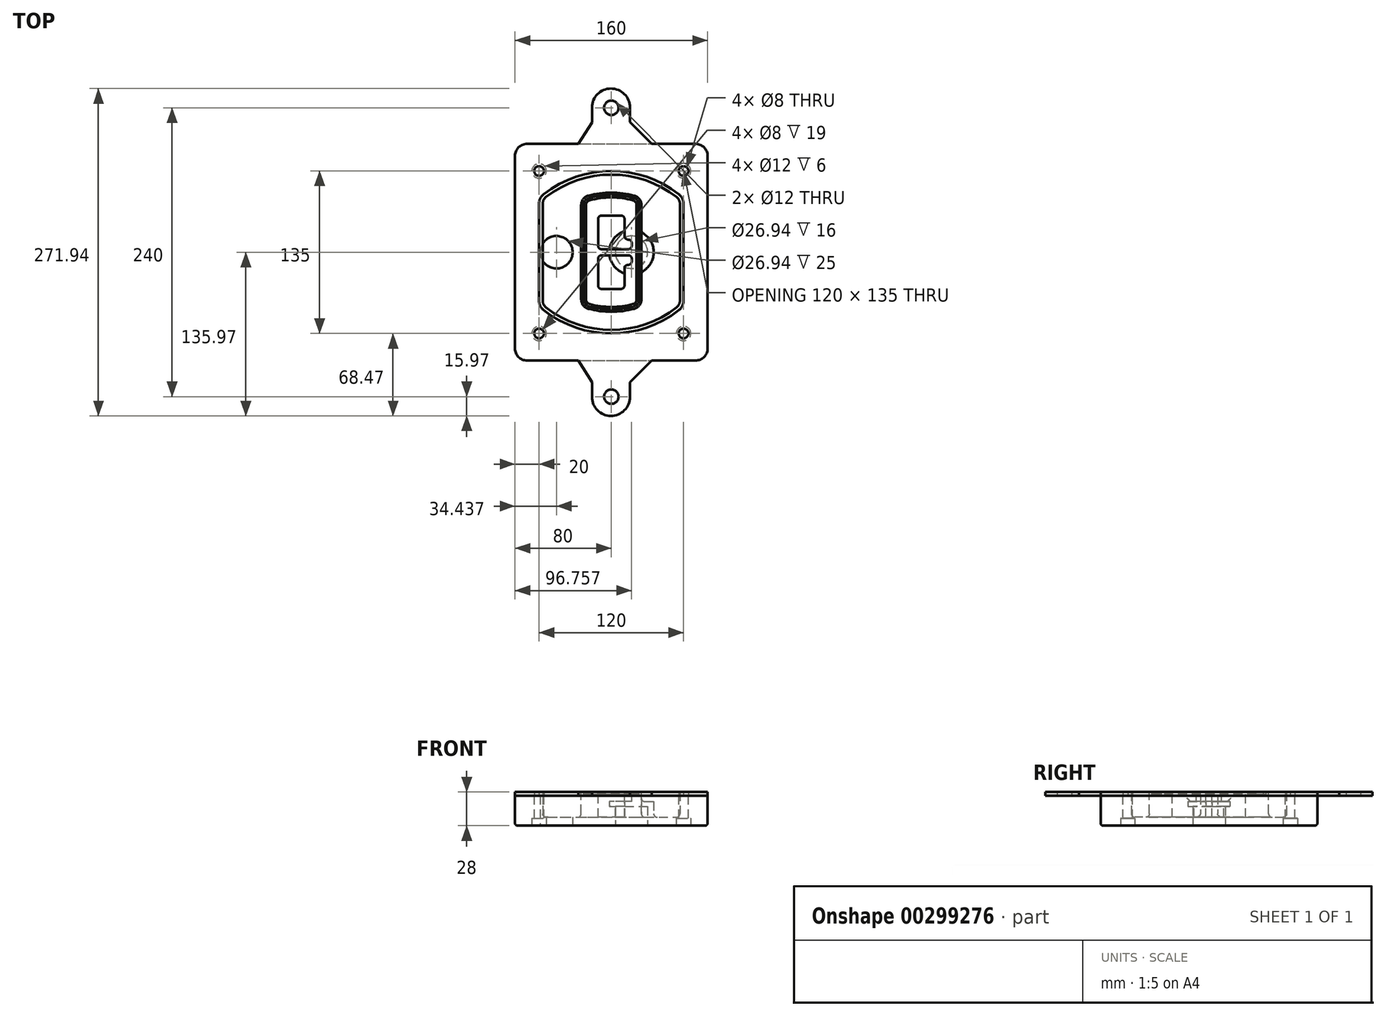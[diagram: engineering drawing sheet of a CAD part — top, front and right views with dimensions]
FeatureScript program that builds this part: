
annotation { "Feature Type Name" : "Feature", "Feature Type Description" : "" }
export const myFeature = defineFeature(function(context is Context, id is Id, definition is map)
    precondition{}
    {
        {
            var Q0;
            Q0=qCreatedBy(makeId("Top.planeOp"),FACE);
            var sketch = newSketch(context, id + "F0", { "sketchPlane" : qUnion([Q0])});
            skPoint(sketch, "E0.rect.middle", {"position": v(0, 0) * mm});
            skLineSegment(sketch, "E1.bottom", {"start": v(-70, -90) * mm, "end": v(70, -90) * mm});
            skLineSegment(sketch, "E1.top", {"start": v(-70, 90) * mm, "end": v(70, 90) * mm});
            skLineSegment(sketch, "E1.left", {"start": v(-80, -80) * mm, "end": v(-80, 80) * mm});
            skLineSegment(sketch, "E1.right", {"start": v(80, -80) * mm, "end": v(80, 80) * mm});
            skLineSegment(sketch, "E2", {"start": v(-80, 90) * mm, "end": v(80, -90) * mm, "construction": true});
            skLineSegment(sketch, "E3", {"start": v(80, 90) * mm, "end": v(-80, -90) * mm, "construction": true});
            skCircle(sketch, "E4", {"center": v(-60, 67.5) * mm, "radius": 4 * mm});
            skCircle(sketch, "E5", {"center": v(60, 67.5) * mm, "radius": 4 * mm});
            skCircle(sketch, "E6", {"center": v(60, -67.5) * mm, "radius": 4 * mm});
            skCircle(sketch, "E7", {"center": v(-60, -67.5) * mm, "radius": 4 * mm});
            skLineSegment(sketch, "E8", {"start": v(-60, 67.5) * mm, "end": v(60, 67.5) * mm, "construction": true});
            skLineSegment(sketch, "E9", {"start": v(60, 67.5) * mm, "end": v(60, -67.5) * mm, "construction": true});
            skLineSegment(sketch, "E10", {"start": v(60, -67.5) * mm, "end": v(-60, -67.5) * mm, "construction": true});
            skLineSegment(sketch, "E11", {"start": v(-60, -67.5) * mm, "end": v(-60, 67.5) * mm, "construction": true});
            skLineSegment(sketch, "E12", {"start": v(-60, 40.3) * mm, "end": v(-60, -40.3) * mm});
            skLineSegment(sketch, "E13", {"start": v(60, 40.3) * mm, "end": v(60, -40.3) * mm});
            skArc(sketch, "E14", {"start": v(56.15, 48.18) * mm, "mid": v(0, 67.5) * mm, "end": v(-56.15, 48.18) * mm});
            skArc(sketch, "E15", {"start": v(-56.15, -48.18) * mm, "mid": v(0, -67.5) * mm, "end": v(56.15, -48.18) * mm});
            skLineSegment(sketch, "E16", {"start": v(-60, 0) * mm, "end": v(60, 0) * mm, "construction": true});
            skPoint(sketch, "E17.visualSharp", {"position": v(-60, -45) * mm});
            skArc(sketch, "E17.filletArc", {"start": v(-60, -40.3) * mm, "mid": v(-58.99, -44.68) * mm, "end": v(-56.15, -48.18) * mm});
            skPoint(sketch, "E18.visualSharp", {"position": v(-60, 45) * mm});
            skArc(sketch, "E18.filletArc", {"start": v(-56.15, 48.18) * mm, "mid": v(-58.99, 44.68) * mm, "end": v(-60, 40.3) * mm});
            skPoint(sketch, "E19.visualSharp", {"position": v(60, 45) * mm});
            skArc(sketch, "E19.filletArc", {"start": v(60, 40.3) * mm, "mid": v(58.99, 44.68) * mm, "end": v(56.15, 48.18) * mm});
            skPoint(sketch, "E20.visualSharp", {"position": v(60, -45) * mm});
            skArc(sketch, "E20.filletArc", {"start": v(56.15, -48.18) * mm, "mid": v(58.99, -44.68) * mm, "end": v(60, -40.3) * mm});
            skPoint(sketch, "E21.visualSharp", {"position": v(-80, 90) * mm});
            skArc(sketch, "E21.filletArc", {"start": v(-70, 90) * mm, "mid": v(-77.07, 87.07) * mm, "end": v(-80, 80) * mm});
            skPoint(sketch, "E22.visualSharp", {"position": v(80, 90) * mm});
            skArc(sketch, "E22.filletArc", {"start": v(80, 80) * mm, "mid": v(77.07, 87.07) * mm, "end": v(70, 90) * mm});
            skPoint(sketch, "E23.visualSharp", {"position": v(80, -90) * mm});
            skArc(sketch, "E23.filletArc", {"start": v(70, -90) * mm, "mid": v(77.07, -87.07) * mm, "end": v(80, -80) * mm});
            skPoint(sketch, "E24.visualSharp", {"position": v(-80, -90) * mm});
            skArc(sketch, "E24.filletArc", {"start": v(-80, -80) * mm, "mid": v(-77.07, -87.07) * mm, "end": v(-70, -90) * mm});
            skArc(sketch, "E25.0", {"start": v(57, 40.3) * mm, "mid": v(56.3, 43.36) * mm, "end": v(54.3, 45.81) * mm});
            skLineSegment(sketch, "E25.1", {"start": v(57, 40.3) * mm, "end": v(57, -40.3) * mm});
            skArc(sketch, "E25.2", {"start": v(54.3, -45.81) * mm, "mid": v(56.3, -43.36) * mm, "end": v(57, -40.3) * mm});
            skArc(sketch, "E25.3", {"start": v(-54.3, -45.81) * mm, "mid": v(0, -64.5) * mm, "end": v(54.3, -45.81) * mm});
            skArc(sketch, "E25.4", {"start": v(-57, -40.3) * mm, "mid": v(-56.3, -43.36) * mm, "end": v(-54.3, -45.81) * mm});
            skArc(sketch, "E25.5", {"start": v(54.3, 45.81) * mm, "mid": v(0, 64.5) * mm, "end": v(-54.3, 45.81) * mm});
            skLineSegment(sketch, "E25.6", {"start": v(-57, 40.3) * mm, "end": v(-57, -40.3) * mm});
            skArc(sketch, "E25.7", {"start": v(-54.3, 45.81) * mm, "mid": v(-56.3, 43.36) * mm, "end": v(-57, 40.3) * mm});
            skArc(sketch, "E26.0", {"start": v(-58.62, 51.33) * mm, "mid": v(-62.58, 46.43) * mm, "end": v(-64, 40.3) * mm});
            skArc(sketch, "E26.1", {"start": v(58.62, 51.33) * mm, "mid": v(0, 71.5) * mm, "end": v(-58.62, 51.33) * mm});
            skArc(sketch, "E26.2", {"start": v(64, 40.3) * mm, "mid": v(62.58, 46.43) * mm, "end": v(58.62, 51.33) * mm});
            skLineSegment(sketch, "E26.3", {"start": v(64, 40.3) * mm, "end": v(64, -40.3) * mm});
            skArc(sketch, "E26.4", {"start": v(58.62, -51.33) * mm, "mid": v(62.58, -46.43) * mm, "end": v(64, -40.3) * mm});
            skLineSegment(sketch, "E26.5", {"start": v(-64, 40.3) * mm, "end": v(-64, -40.3) * mm});
            skArc(sketch, "E26.6", {"start": v(-58.62, -51.33) * mm, "mid": v(0, -71.5) * mm, "end": v(58.62, -51.33) * mm});
            skArc(sketch, "E26.7", {"start": v(-64, -40.3) * mm, "mid": v(-62.58, -46.43) * mm, "end": v(-58.62, -51.33) * mm});
            skSolve(sketch);
        }
        {
            var Q0;
            Q0=makeQuery(id+"F0.imprint","IMPRINT",FACE,{"disambiguationData":[TD([[makeQuery(id+"F0.imprint","IMPRINT",EDGE,{"derivedFrom":sQuery(id+"F0.wireOp",EDGE,"E1.bottom")}),1.0]])]});
            var Q1;
            Q1=makeQuery(id+"F0.imprint","IMPRINT",FACE,{"disambiguationData":[TD([[makeQuery(id+"F0.imprint","IMPRINT",EDGE,{"derivedFrom":sQuery(id+"F0.wireOp",EDGE,"E12")}),1.0]])]});
            var Q2;
            Q2=makeQuery(id+"F0.imprint","IMPRINT",FACE,{"disambiguationData":[TD([[makeQuery(id+"F0.imprint","IMPRINT",EDGE,{"derivedFrom":sQuery(id+"F0.wireOp",EDGE,"E25.0")}),1.0]])]});
            var Q3;
            Q3=makeQuery(id+"F0.imprint","IMPRINT",FACE,{"disambiguationData":[TD([[makeQuery(id+"F0.imprint","IMPRINT",EDGE,{"derivedFrom":sQuery(id+"F0.wireOp",EDGE,"E12")}),-1.0]])]});
            extrude(context, id + "F1", {"entities" : qUnion([Q0, Q1, Q2, Q3]), "oppositeDirection" : true, "depth" : 25 * mm});
        }
        {
            var Q0;
            Q0=makeQuery(id+"F0.imprint","IMPRINT",FACE,{"disambiguationData":[TD([[makeQuery(id+"F0.imprint","IMPRINT",EDGE,{"derivedFrom":sQuery(id+"F0.wireOp",EDGE,"E12")}),1.0]])]});
            extrude(context, id + "F2", {"entities" : qUnion([Q0]), "operationType" : NewBodyOperationType.ADD, "depth" : 3 * mm});
        }
        {
            var Q0;
            Q0=makeQuery(id+"F0.imprint","IMPRINT",FACE,{"disambiguationData":[TD([[makeQuery(id+"F0.imprint","IMPRINT",EDGE,{"derivedFrom":sQuery(id+"F0.wireOp",EDGE,"E25.0")}),1.0]])]});
            extrude(context, id + "F3", {"entities" : qUnion([Q0]), "operationType" : NewBodyOperationType.REMOVE, "oppositeDirection" : true, "depth" : 18 * mm});
        }
        {
            var Q0;
            Q0=makeQuery(id+"F2.opExtrude","CAP_FACE",FACE,{"disambiguationData":[OSD([sQuery(id+"F0.wireOp",EDGE,"E12"),sQuery(id+"F0.wireOp",EDGE,"E13"),sQuery(id+"F0.wireOp",EDGE,"E14"),sQuery(id+"F0.wireOp",EDGE,"E15"),sQuery(id+"F0.wireOp",EDGE,"E17.filletArc"),sQuery(id+"F0.wireOp",EDGE,"E18.filletArc"),sQuery(id+"F0.wireOp",EDGE,"E19.filletArc"),sQuery(id+"F0.wireOp",EDGE,"E20.filletArc"),sQuery(id+"F0.wireOp",EDGE,"E25.0"),sQuery(id+"F0.wireOp",EDGE,"E25.1"),sQuery(id+"F0.wireOp",EDGE,"E25.2"),sQuery(id+"F0.wireOp",EDGE,"E25.3"),sQuery(id+"F0.wireOp",EDGE,"E25.4"),sQuery(id+"F0.wireOp",EDGE,"E25.5"),sQuery(id+"F0.wireOp",EDGE,"E25.6"),sQuery(id+"F0.wireOp",EDGE,"E25.7")])],"isStart":false});
            var sketch = newSketch(context, id + "F4", { "sketchPlane" : qUnion([Q0])});
            skArc(sketch, "E27.0", {"start": v(-19.08, -46.97) * mm, "mid": v(0, -49.5) * mm, "end": v(19.08, -46.97) * mm});
            skArc(sketch, "E28.0", {"start": v(19.08, 46.97) * mm, "mid": v(0, 49.5) * mm, "end": v(-19.08, 46.97) * mm});
            skLineSegment(sketch, "E29", {"start": v(-25, 39.25) * mm, "end": v(-25, -39.25) * mm});
            skLineSegment(sketch, "E30", {"start": v(25, 39.25) * mm, "end": v(25, -39.25) * mm});
            skLineSegment(sketch, "E31", {"start": v(-25, 45.1) * mm, "end": v(25, 45.1) * mm, "construction": true});
            skLineSegment(sketch, "E32", {"start": v(-25, -45.1) * mm, "end": v(25, -45.1) * mm, "construction": true});
            skPoint(sketch, "E33.visualSharp", {"position": v(-25, 45.1) * mm});
            skArc(sketch, "E33.filletArc", {"start": v(-19.08, 46.97) * mm, "mid": v(-23.35, 44.11) * mm, "end": v(-25, 39.25) * mm});
            skPoint(sketch, "E34.visualSharp", {"position": v(25, 45.1) * mm});
            skArc(sketch, "E34.filletArc", {"start": v(25, 39.25) * mm, "mid": v(23.35, 44.11) * mm, "end": v(19.08, 46.97) * mm});
            skPoint(sketch, "E35.visualSharp", {"position": v(25, -45.1) * mm});
            skArc(sketch, "E35.filletArc", {"start": v(19.08, -46.97) * mm, "mid": v(23.35, -44.11) * mm, "end": v(25, -39.25) * mm});
            skPoint(sketch, "E36.visualSharp", {"position": v(-25, -45.1) * mm});
            skArc(sketch, "E36.filletArc", {"start": v(-25, -39.25) * mm, "mid": v(-23.35, -44.11) * mm, "end": v(-19.08, -46.97) * mm});
            skArc(sketch, "E37.0", {"start": v(54.3, 45.81) * mm, "mid": v(0, 64.5) * mm, "end": v(-54.3, 45.81) * mm});
            skArc(sketch, "E37.1", {"start": v(-54.3, 45.81) * mm, "mid": v(-56.3, 43.36) * mm, "end": v(-57, 40.3) * mm});
            skLineSegment(sketch, "E37.2", {"start": v(-57, 40.3) * mm, "end": v(-57, -40.3) * mm});
            skArc(sketch, "E37.3", {"start": v(-57, -40.3) * mm, "mid": v(-56.3, -43.36) * mm, "end": v(-54.3, -45.81) * mm});
            skArc(sketch, "E37.4", {"start": v(-54.3, -45.81) * mm, "mid": v(0, -64.5) * mm, "end": v(54.3, -45.81) * mm});
            skArc(sketch, "E37.5", {"start": v(54.3, -45.81) * mm, "mid": v(56.3, -43.36) * mm, "end": v(57, -40.3) * mm});
            skLineSegment(sketch, "E37.6", {"start": v(57, 40.3) * mm, "end": v(57, -40.3) * mm});
            skArc(sketch, "E37.7", {"start": v(57, 40.3) * mm, "mid": v(56.3, 43.36) * mm, "end": v(54.3, 45.81) * mm});
            skLineSegment(sketch, "E38.0", {"start": v(23, 39.25) * mm, "end": v(23, -39.25) * mm});
            skArc(sketch, "E38.1", {"start": v(18.56, -45.04) * mm, "mid": v(21.76, -42.9) * mm, "end": v(23, -39.25) * mm});
            skArc(sketch, "E38.2", {"start": v(-18.56, -45.04) * mm, "mid": v(0, -47.5) * mm, "end": v(18.56, -45.04) * mm});
            skArc(sketch, "E38.3", {"start": v(-23, -39.25) * mm, "mid": v(-21.76, -42.9) * mm, "end": v(-18.56, -45.04) * mm});
            skLineSegment(sketch, "E38.4", {"start": v(-23, 39.25) * mm, "end": v(-23, -39.25) * mm});
            skArc(sketch, "E38.5", {"start": v(23, 39.25) * mm, "mid": v(21.76, 42.9) * mm, "end": v(18.56, 45.04) * mm});
            skArc(sketch, "E38.6", {"start": v(-18.56, 45.04) * mm, "mid": v(-21.76, 42.9) * mm, "end": v(-23, 39.25) * mm});
            skArc(sketch, "E38.7", {"start": v(18.56, 45.04) * mm, "mid": v(0, 47.5) * mm, "end": v(-18.56, 45.04) * mm});
            skArc(sketch, "E39.0", {"start": v(21, 39.25) * mm, "mid": v(20.18, 41.68) * mm, "end": v(18.04, 43.1) * mm});
            skLineSegment(sketch, "E39.1", {"start": v(21, 39.25) * mm, "end": v(21, -39.25) * mm});
            skArc(sketch, "E39.2", {"start": v(18.04, -43.1) * mm, "mid": v(20.18, -41.68) * mm, "end": v(21, -39.25) * mm});
            skArc(sketch, "E39.3", {"start": v(-18.04, -43.1) * mm, "mid": v(0, -45.5) * mm, "end": v(18.04, -43.1) * mm});
            skArc(sketch, "E39.4", {"start": v(-21, -39.25) * mm, "mid": v(-20.18, -41.68) * mm, "end": v(-18.04, -43.1) * mm});
            skArc(sketch, "E39.5", {"start": v(18.04, 43.1) * mm, "mid": v(0, 45.5) * mm, "end": v(-18.04, 43.1) * mm});
            skLineSegment(sketch, "E39.6", {"start": v(-21, 39.25) * mm, "end": v(-21, -39.25) * mm});
            skArc(sketch, "E39.7", {"start": v(-18.04, 43.1) * mm, "mid": v(-20.18, 41.68) * mm, "end": v(-21, 39.25) * mm});
            skLineSegment(sketch, "E40", {"start": v(-25, 0) * mm, "end": v(25, 0) * mm, "construction": true});
            skLineSegment(sketch, "E41", {"start": v(-11, 5.5) * mm, "end": v(-11, 27.5) * mm});
            skLineSegment(sketch, "E42", {"start": v(-8, 30.5) * mm, "end": v(8, 30.5) * mm});
            skLineSegment(sketch, "E43", {"start": v(11, 27.5) * mm, "end": v(11, 13.5) * mm});
            skLineSegment(sketch, "E44", {"start": v(14, 10.5) * mm, "end": v(14, 10.5) * mm});
            skLineSegment(sketch, "E45", {"start": v(17, 7.5) * mm, "end": v(17, 5.5) * mm});
            skLineSegment(sketch, "E46", {"start": v(14, 2.5) * mm, "end": v(-8, 2.5) * mm});
            skPoint(sketch, "E47.visualSharp", {"position": v(-11, 30.5) * mm});
            skArc(sketch, "E47.filletArc", {"start": v(-8, 30.5) * mm, "mid": v(-10.12, 29.62) * mm, "end": v(-11, 27.5) * mm});
            skPoint(sketch, "E48.visualSharp", {"position": v(11, 30.5) * mm});
            skArc(sketch, "E48.filletArc", {"start": v(11, 27.5) * mm, "mid": v(10.12, 29.62) * mm, "end": v(8, 30.5) * mm});
            skPoint(sketch, "E49.visualSharp", {"position": v(11, 10.5) * mm});
            skArc(sketch, "E49.filletArc", {"start": v(11, 13.5) * mm, "mid": v(11.88, 11.38) * mm, "end": v(14, 10.5) * mm});
            skPoint(sketch, "E50.visualSharp", {"position": v(17, 10.5) * mm});
            skArc(sketch, "E50.filletArc", {"start": v(17, 7.5) * mm, "mid": v(16.12, 9.62) * mm, "end": v(14, 10.5) * mm});
            skPoint(sketch, "E51.visualSharp", {"position": v(17, 2.5) * mm});
            skArc(sketch, "E51.filletArc", {"start": v(14, 2.5) * mm, "mid": v(16.12, 3.38) * mm, "end": v(17, 5.5) * mm});
            skPoint(sketch, "E52.visualSharp", {"position": v(-11, 2.5) * mm});
            skArc(sketch, "E52.filletArc", {"start": v(-11, 5.5) * mm, "mid": v(-10.12, 3.38) * mm, "end": v(-8, 2.5) * mm});
            skLineSegment(sketch, "E53.0.MirrorCS", {"start": v(14, -2.5) * mm, "end": v(-8, -2.5) * mm});
            skArc(sketch, "E54.0.MirrorCS", {"start": v(-11, -5.5) * mm, "mid": v(-10.12, -3.38) * mm, "end": v(-8, -2.5) * mm});
            skLineSegment(sketch, "E55.0.MirrorCS", {"start": v(-11, -5.5) * mm, "end": v(-11, -27.5) * mm});
            skArc(sketch, "E56.0.MirrorCS", {"start": v(-8, -30.5) * mm, "mid": v(-10.12, -29.62) * mm, "end": v(-11, -27.5) * mm});
            skLineSegment(sketch, "E57.0.MirrorCS", {"start": v(-8, -30.5) * mm, "end": v(8, -30.5) * mm});
            skArc(sketch, "E58.0.MirrorCS", {"start": v(11, -27.5) * mm, "mid": v(10.12, -29.62) * mm, "end": v(8, -30.5) * mm});
            skLineSegment(sketch, "E59.0.MirrorCS", {"start": v(11, -27.5) * mm, "end": v(11, -13.5) * mm});
            skArc(sketch, "E60.0.MirrorCS", {"start": v(11, -13.5) * mm, "mid": v(11.88, -11.38) * mm, "end": v(14, -10.5) * mm});
            skArc(sketch, "E61.0.MirrorCS", {"start": v(17, -7.5) * mm, "mid": v(16.12, -9.62) * mm, "end": v(14, -10.5) * mm});
            skLineSegment(sketch, "E62.0.MirrorCS", {"start": v(17, -7.5) * mm, "end": v(17, -5.5) * mm});
            skArc(sketch, "E63.0.MirrorCS", {"start": v(14, -2.5) * mm, "mid": v(16.12, -3.38) * mm, "end": v(17, -5.5) * mm});
            skSolve(sketch);
        }
        {
            var Q0;
            Q0=makeQuery(id+"F4.imprint","IMPRINT",FACE,{"disambiguationData":[TD([[makeQuery(id+"F4.imprint","IMPRINT",EDGE,{"derivedFrom":sQuery(id+"F4.wireOp",EDGE,"E27.0")}),1.0]])]});
            var Q1;
            Q1=makeQuery(id+"F4.imprint","IMPRINT",FACE,{"disambiguationData":[TD([[makeQuery(id+"F4.imprint","IMPRINT",EDGE,{"derivedFrom":sQuery(id+"F4.wireOp",EDGE,"E38.0")}),-1.0]])]});
            var Q2;
            Q2=makeQuery(id+"F4.imprint","IMPRINT",FACE,{"disambiguationData":[TD([[makeQuery(id+"F4.imprint","IMPRINT",EDGE,{"derivedFrom":sQuery(id+"F4.wireOp",EDGE,"E39.0")}),1.0]])]});
            extrude(context, id + "F5", {"entities" : qUnion([Q0, Q1, Q2]), "operationType" : NewBodyOperationType.ADD, "endBound" : BoundingType.UP_TO_NEXT, "oppositeDirection" : true, "depth" : 25 * mm});
        }
        {
            var Q0;
            Q0=makeQuery(id+"F4.imprint","IMPRINT",FACE,{"disambiguationData":[TD([[makeQuery(id+"F4.imprint","IMPRINT",EDGE,{"derivedFrom":sQuery(id+"F4.wireOp",EDGE,"E38.0")}),-1.0]])]});
            extrude(context, id + "F6", {"entities" : qUnion([Q0]), "operationType" : NewBodyOperationType.REMOVE, "oppositeDirection" : true, "depth" : 2 * mm});
        }
        {
            var Q0;
            Q0=makeQuery(id+"F1.opExtrude","CAP_FACE",FACE,{"disambiguationData":[OSD([sQuery(id+"F0.wireOp",EDGE,"E1.bottom"),sQuery(id+"F0.wireOp",EDGE,"E1.top"),sQuery(id+"F0.wireOp",EDGE,"E1.left"),sQuery(id+"F0.wireOp",EDGE,"E1.right"),sQuery(id+"F0.wireOp",EDGE,"E4"),sQuery(id+"F0.wireOp",EDGE,"E5"),sQuery(id+"F0.wireOp",EDGE,"E6"),sQuery(id+"F0.wireOp",EDGE,"E7"),sQuery(id+"F0.wireOp",EDGE,"E21.filletArc"),sQuery(id+"F0.wireOp",EDGE,"E22.filletArc"),sQuery(id+"F0.wireOp",EDGE,"E23.filletArc"),sQuery(id+"F0.wireOp",EDGE,"E24.filletArc")])],"isStart":false});
            var sketch = newSketch(context, id + "F7", { "sketchPlane" : qUnion([Q0])});
            skCircle(sketch, "E64", {"center": v(16.76, 0) * mm, "radius": 13.47 * mm});
            skCircle(sketch, "E65", {"center": v(-45.56, 0) * mm, "radius": 13.47 * mm});
            skLineSegment(sketch, "E66", {"start": v(80, 0) * mm, "end": v(-80, 0) * mm});
            skCircle(sketch, "E67", {"center": v(16.76, 0) * mm, "radius": 18.47 * mm});
            skCircle(sketch, "E68", {"center": v(60, -67.5) * mm, "radius": 6 * mm});
            skCircle(sketch, "E69", {"center": v(-60, -67.5) * mm, "radius": 6 * mm});
            skCircle(sketch, "E70", {"center": v(-60, 67.5) * mm, "radius": 6 * mm});
            skCircle(sketch, "E71", {"center": v(60, 67.5) * mm, "radius": 6 * mm});
            skSolve(sketch);
        }
        {
            var Q0;
            {var subQ1=sQuery(id+"F7.wireOp",EDGE,"E66");var subQ4=sQuery(id+"F7.wireOp",EDGE,"E64");var subQ6=makeQuery(id+"F7.imprint","INTERSECT",VERTEX,{"disambiguationData":[OD(0.0)],"derivedFrom":[subQ4,subQ1]});Q0=makeQuery(id+"F7.imprint","IMPRINT",FACE,{"disambiguationData":[TD([[makeQuery(id+"F7.imprint","IMPRINT",EDGE,{"disambiguationData":[TD([[subQ6,-1.0]])],"derivedFrom":subQ4}),-1.0]])]});}
            var Q1;
            {var subQ0=sQuery(id+"F7.wireOp",EDGE,"E66");var subQ1=sQuery(id+"F7.wireOp",EDGE,"E64");var subQ3=makeQuery(id+"F7.imprint","INTERSECT",VERTEX,{"disambiguationData":[OD(0.0)],"derivedFrom":[subQ1,subQ0]});Q1=makeQuery(id+"F7.imprint","IMPRINT",FACE,{"disambiguationData":[TD([[makeQuery(id+"F7.imprint","IMPRINT",EDGE,{"disambiguationData":[TD([[subQ3,-1.0]])],"derivedFrom":subQ1}),1.0]])]});}
            var Q2;
            {var subQ0=sQuery(id+"F7.wireOp",EDGE,"E66");var subQ1=sQuery(id+"F7.wireOp",EDGE,"E64");var subQ3=makeQuery(id+"F7.imprint","INTERSECT",VERTEX,{"disambiguationData":[OD(0.0)],"derivedFrom":[subQ1,subQ0]});Q2=makeQuery(id+"F7.imprint","IMPRINT",FACE,{"disambiguationData":[TD([[makeQuery(id+"F7.imprint","IMPRINT",EDGE,{"disambiguationData":[TD([[subQ3,1.0]])],"derivedFrom":subQ1}),1.0]])]});}
            var Q3;
            {var subQ1=sQuery(id+"F7.wireOp",EDGE,"E66");var subQ4=sQuery(id+"F7.wireOp",EDGE,"E64");var subQ6=makeQuery(id+"F7.imprint","INTERSECT",VERTEX,{"disambiguationData":[OD(0.0)],"derivedFrom":[subQ4,subQ1]});Q3=makeQuery(id+"F7.imprint","IMPRINT",FACE,{"disambiguationData":[TD([[makeQuery(id+"F7.imprint","IMPRINT",EDGE,{"disambiguationData":[TD([[subQ6,1.0]])],"derivedFrom":subQ4}),-1.0]])]});}
            extrude(context, id + "F8", {"entities" : qUnion([Q0, Q1, Q2, Q3]), "operationType" : NewBodyOperationType.ADD, "oppositeDirection" : true, "depth" : 20 * mm});
        }
        {
            var Q0;
            {var subQ0=sQuery(id+"F7.wireOp",EDGE,"E66");var subQ1=sQuery(id+"F7.wireOp",EDGE,"E64");var subQ3=makeQuery(id+"F7.imprint","INTERSECT",VERTEX,{"disambiguationData":[OD(0.0)],"derivedFrom":[subQ1,subQ0]});Q0=makeQuery(id+"F7.imprint","IMPRINT",FACE,{"disambiguationData":[TD([[makeQuery(id+"F7.imprint","IMPRINT",EDGE,{"disambiguationData":[TD([[subQ3,-1.0]])],"derivedFrom":subQ1}),1.0]])]});}
            var Q1;
            {var subQ0=sQuery(id+"F7.wireOp",EDGE,"E66");var subQ1=sQuery(id+"F7.wireOp",EDGE,"E64");var subQ3=makeQuery(id+"F7.imprint","INTERSECT",VERTEX,{"disambiguationData":[OD(0.0)],"derivedFrom":[subQ1,subQ0]});Q1=makeQuery(id+"F7.imprint","IMPRINT",FACE,{"disambiguationData":[TD([[makeQuery(id+"F7.imprint","IMPRINT",EDGE,{"disambiguationData":[TD([[subQ3,1.0]])],"derivedFrom":subQ1}),1.0]])]});}
            extrude(context, id + "F9", {"entities" : qUnion([Q0, Q1]), "operationType" : NewBodyOperationType.REMOVE, "oppositeDirection" : true, "depth" : 16 * mm});
        }
        {
            var Q0;
            {var subQ0=sQuery(id+"F7.wireOp",EDGE,"E66");var subQ1=sQuery(id+"F7.wireOp",EDGE,"E65");var subQ3=makeQuery(id+"F7.imprint","INTERSECT",VERTEX,{"disambiguationData":[OD(0.0)],"derivedFrom":[subQ1,subQ0]});Q0=makeQuery(id+"F7.imprint","IMPRINT",FACE,{"disambiguationData":[TD([[makeQuery(id+"F7.imprint","IMPRINT",EDGE,{"disambiguationData":[TD([[subQ3,-1.0]])],"derivedFrom":subQ1}),1.0]])]});}
            var Q1;
            {var subQ0=sQuery(id+"F7.wireOp",EDGE,"E66");var subQ1=sQuery(id+"F7.wireOp",EDGE,"E65");var subQ3=makeQuery(id+"F7.imprint","INTERSECT",VERTEX,{"disambiguationData":[OD(0.0)],"derivedFrom":[subQ1,subQ0]});Q1=makeQuery(id+"F7.imprint","IMPRINT",FACE,{"disambiguationData":[TD([[makeQuery(id+"F7.imprint","IMPRINT",EDGE,{"disambiguationData":[TD([[subQ3,1.0]])],"derivedFrom":subQ1}),1.0]])]});}
            extrude(context, id + "F10", {"entities" : qUnion([Q0, Q1]), "operationType" : NewBodyOperationType.REMOVE, "oppositeDirection" : true, "depth" : 25 * mm});
        }
        {
            var Q0;
            Q0=makeQuery(id+"F7.imprint","IMPRINT",FACE,{"disambiguationData":[TD([[makeQuery(id+"F7.imprint","IMPRINT",EDGE,{"derivedFrom":sQuery(id+"F7.wireOp",EDGE,"E68")}),1.0]])]});
            var Q1;
            Q1=makeQuery(id+"F7.imprint","IMPRINT",FACE,{"disambiguationData":[TD([[makeQuery(id+"F7.imprint","IMPRINT",EDGE,{"derivedFrom":makeQuery(id+"F1.opExtrude","CAP_EDGE",EDGE,{"disambiguationData":[OSD([sQuery(id+"F0.wireOp",EDGE,"E5")])],"isStart":false})}),-1.0]])]});
            var Q2;
            Q2=makeQuery(id+"F7.imprint","IMPRINT",FACE,{"disambiguationData":[TD([[makeQuery(id+"F7.imprint","IMPRINT",EDGE,{"derivedFrom":sQuery(id+"F7.wireOp",EDGE,"E69")}),1.0]])]});
            var Q3;
            Q3=makeQuery(id+"F7.imprint","IMPRINT",FACE,{"disambiguationData":[TD([[makeQuery(id+"F7.imprint","IMPRINT",EDGE,{"derivedFrom":makeQuery(id+"F1.opExtrude","CAP_EDGE",EDGE,{"disambiguationData":[OSD([sQuery(id+"F0.wireOp",EDGE,"E4")])],"isStart":false})}),-1.0]])]});
            var Q4;
            Q4=makeQuery(id+"F7.imprint","IMPRINT",FACE,{"disambiguationData":[TD([[makeQuery(id+"F7.imprint","IMPRINT",EDGE,{"derivedFrom":sQuery(id+"F7.wireOp",EDGE,"E70")}),1.0]])]});
            var Q5;
            Q5=makeQuery(id+"F7.imprint","IMPRINT",FACE,{"disambiguationData":[TD([[makeQuery(id+"F7.imprint","IMPRINT",EDGE,{"derivedFrom":makeQuery(id+"F1.opExtrude","CAP_EDGE",EDGE,{"disambiguationData":[OSD([sQuery(id+"F0.wireOp",EDGE,"E7")])],"isStart":false})}),-1.0]])]});
            var Q6;
            Q6=makeQuery(id+"F7.imprint","IMPRINT",FACE,{"disambiguationData":[TD([[makeQuery(id+"F7.imprint","IMPRINT",EDGE,{"derivedFrom":sQuery(id+"F7.wireOp",EDGE,"E71")}),1.0]])]});
            var Q7;
            Q7=makeQuery(id+"F7.imprint","IMPRINT",FACE,{"disambiguationData":[TD([[makeQuery(id+"F7.imprint","IMPRINT",EDGE,{"derivedFrom":makeQuery(id+"F1.opExtrude","CAP_EDGE",EDGE,{"disambiguationData":[OSD([sQuery(id+"F0.wireOp",EDGE,"E6")])],"isStart":false})}),-1.0]])]});
            extrude(context, id + "F11", {"entities" : qUnion([Q0, Q1, Q2, Q3, Q4, Q5, Q6, Q7]), "operationType" : NewBodyOperationType.REMOVE, "oppositeDirection" : true, "depth" : 6 * mm});
        }
        {
            var Q0;
            Q0=makeQuery(id+"F9.boolean.opBoolean","COPY",FACE,{"derivedFrom":makeQuery(id+"F9.opExtrude","CAP_FACE",FACE,{"disambiguationData":[OSD([sQuery(id+"F7.wireOp",EDGE,"E64")])],"isStart":false})});
            var sketch = newSketch(context, id + "F12", { "sketchPlane" : qUnion([Q0])});
            skArc(sketch, "E72.0", {"start": v(11, 17.55) * mm, "mid": v(2.57, 11.82) * mm, "end": v(-1.54, 2.5) * mm});
            skArc(sketch, "E72.1", {"start": v(-1.54, -2.5) * mm, "mid": v(2.57, -11.82) * mm, "end": v(11, -17.55) * mm});
            skLineSegment(sketch, "E73", {"start": v(-1.54, -2.5) * mm, "end": v(14, -2.5) * mm});
            skLineSegment(sketch, "E74.0", {"start": v(14, 2.5) * mm, "end": v(-1.54, 2.5) * mm});
            skArc(sketch, "E74.1", {"start": v(14, 2.5) * mm, "mid": v(16.12, 3.38) * mm, "end": v(17, 5.5) * mm});
            skLineSegment(sketch, "E74.2", {"start": v(17, 7.5) * mm, "end": v(17, 5.5) * mm});
            skArc(sketch, "E74.3", {"start": v(17, 7.5) * mm, "mid": v(16.12, 9.62) * mm, "end": v(14, 10.5) * mm});
            skArc(sketch, "E74.4", {"start": v(11, 13.5) * mm, "mid": v(11.88, 11.38) * mm, "end": v(14, 10.5) * mm});
            skLineSegment(sketch, "E74.5", {"start": v(11, 17.55) * mm, "end": v(11, 13.5) * mm});
            skLineSegment(sketch, "E74.7", {"start": v(14, -2.5) * mm, "end": v(-1.54, -2.5) * mm});
            skArc(sketch, "E74.8", {"start": v(14, -2.5) * mm, "mid": v(16.12, -3.38) * mm, "end": v(17, -5.5) * mm});
            skLineSegment(sketch, "E74.9", {"start": v(17, -7.5) * mm, "end": v(17, -5.5) * mm});
            skArc(sketch, "E74.10", {"start": v(17, -7.5) * mm, "mid": v(16.12, -9.62) * mm, "end": v(14, -10.5) * mm});
            skArc(sketch, "E74.11", {"start": v(11, -13.5) * mm, "mid": v(11.88, -11.38) * mm, "end": v(14, -10.5) * mm});
            skLineSegment(sketch, "E74.12", {"start": v(11, -17.55) * mm, "end": v(11, -13.5) * mm});
            skPoint(sketch, "E75.orphan", {"position": v(11, -27.5) * mm});
            skPoint(sketch, "E76.orphan", {"position": v(-8, -2.5) * mm});
            skPoint(sketch, "E77.orphan", {"position": v(-8, 2.5) * mm});
            skPoint(sketch, "E78.orphan", {"position": v(11, 27.5) * mm});
            skSolve(sketch);
        }
        {
            var Q0;
            {var subQ7=sQuery(id+"F12.wireOp",EDGE,"E72.0");var subQ14=sQuery(id+"F12.wireOp",EDGE,"E72.1");var subQ16=sQuery(id+"F12.wireOp",EDGE,"E74.1");var subQ18=sQuery(id+"F12.wireOp",EDGE,"E74.8");Q0=qUnion([makeQuery(id+"F12.imprint","IMPRINT",FACE,{"disambiguationData":[TD([[makeQuery(id+"F12.imprint","IMPRINT",EDGE,{"derivedFrom":subQ7}),1.0]])]}),makeQuery(id+"F12.imprint","IMPRINT",FACE,{"disambiguationData":[TD([[makeQuery(id+"F12.imprint","IMPRINT",EDGE,{"derivedFrom":subQ14}),1.0]])]}),makeQuery(id+"F12.imprint","IMPRINT",FACE,{"disambiguationData":[TD([[makeQuery(id+"F12.imprint","IMPRINT",EDGE,{"derivedFrom":subQ16}),1.0]])]}),makeQuery(id+"F12.imprint","IMPRINT",FACE,{"disambiguationData":[TD([[makeQuery(id+"F12.imprint","IMPRINT",EDGE,{"derivedFrom":subQ18}),-1.0]])]})]);}
            var Q1;
            Q1=makeQuery(id+"F5.boolean.opBoolean","SPLIT",FACE,{"disambiguationData":[TD([makeQuery(id+"F5.opExtrude","SWEPT_FACE",FACE,{"disambiguationData":[OSD([sQuery(id+"F4.wireOp",EDGE,"E41")])]})])],"derivedFrom":makeQuery(id+"F3.boolean.opBoolean","COPY",FACE,{"derivedFrom":makeQuery(id+"F3.opExtrude","CAP_FACE",FACE,{"disambiguationData":[OSD([sQuery(id+"F0.wireOp",EDGE,"E25.0"),sQuery(id+"F0.wireOp",EDGE,"E25.1"),sQuery(id+"F0.wireOp",EDGE,"E25.2"),sQuery(id+"F0.wireOp",EDGE,"E25.3"),sQuery(id+"F0.wireOp",EDGE,"E25.4"),sQuery(id+"F0.wireOp",EDGE,"E25.5"),sQuery(id+"F0.wireOp",EDGE,"E25.6"),sQuery(id+"F0.wireOp",EDGE,"E25.7")])],"isStart":false})})});
            extrude(context, id + "F13", {"entities" : qUnion([Q0]), "operationType" : NewBodyOperationType.REMOVE, "endBound" : BoundingType.UP_TO_SURFACE, "endBoundEntityFace" : qUnion([Q1]), "depth" : 25 * mm});
        }
        {
            var Q0;
            Q0=makeQuery(id+"F3.boolean.opBoolean","COPY",EDGE,{"derivedFrom":makeQuery(id+"F3.opExtrude","CAP_EDGE",EDGE,{"disambiguationData":[OSD([sQuery(id+"F0.wireOp",EDGE,"E25.6")])],"isStart":false})});
            var Q1;
            Q1=makeQuery(id+"F8.boolean.opBoolean","INTERSECT",EDGE,{"derivedFrom":[makeQuery(id+"F5.opExtrude","SWEPT_FACE",FACE,{"disambiguationData":[OSD([sQuery(id+"F4.wireOp",EDGE,"E30")])]}),makeQuery(id+"F8.opExtrude","CAP_FACE",FACE,{"disambiguationData":[OSD([sQuery(id+"F7.wireOp",EDGE,"E67")])],"isStart":false})]});
            var Q2;
            Q2=makeQuery(id+"F8.boolean.opBoolean","INTERSECT",EDGE,{"disambiguationData":[OD(1.0)],"derivedFrom":[makeQuery(id+"F5.opExtrude","SWEPT_FACE",FACE,{"disambiguationData":[OSD([sQuery(id+"F4.wireOp",EDGE,"E30")])]}),makeQuery(id+"F8.opExtrude","SWEPT_FACE",FACE,{"disambiguationData":[OSD([sQuery(id+"F7.wireOp",EDGE,"E67")])]})]});
            var Q3;
            {var subQ0=sQuery(id+"F4.wireOp",EDGE,"E30");Q3=makeQuery(id+"F8.boolean.opBoolean","SPLIT",EDGE,{"disambiguationData":[TD([makeQuery(id+"F5.opExtrude","SWEPT_FACE",FACE,{"disambiguationData":[OSD([sQuery(id+"F4.wireOp",EDGE,"E35.filletArc")])]})])],"derivedFrom":makeQuery(id+"F5.opExtrude","CAP_EDGE",EDGE,{"disambiguationData":[OSD([subQ0])],"isStart":false})});}
            var Q4;
            {var subQ0=sQuery(id+"F0.wireOp",EDGE,"E25.7");var subQ1=sQuery(id+"F0.wireOp",EDGE,"E25.1");var subQ2=sQuery(id+"F0.wireOp",EDGE,"E25.6");var subQ3=sQuery(id+"F0.wireOp",EDGE,"E25.5");var subQ4=sQuery(id+"F0.wireOp",EDGE,"E25.4");var subQ5=sQuery(id+"F0.wireOp",EDGE,"E25.0");var subQ6=sQuery(id+"F0.wireOp",EDGE,"E25.2");var subQ7=sQuery(id+"F0.wireOp",EDGE,"E25.3");Q4=makeQuery(id+"F8.boolean.opBoolean","INTERSECT",EDGE,{"derivedFrom":[makeQuery(id+"F5.boolean.opBoolean","SPLIT",FACE,{"disambiguationData":[TD([makeQuery(id+"F2.opExtrude","SWEPT_FACE",FACE,{"disambiguationData":[OSD([subQ5])]})])],"derivedFrom":makeQuery(id+"F3.boolean.opBoolean","COPY",FACE,{"derivedFrom":makeQuery(id+"F3.opExtrude","CAP_FACE",FACE,{"disambiguationData":[OSD([subQ5,subQ1,subQ6,subQ7,subQ4,subQ3,subQ2,subQ0])],"isStart":false})})}),makeQuery(id+"F8.opExtrude","SWEPT_FACE",FACE,{"disambiguationData":[OSD([sQuery(id+"F7.wireOp",EDGE,"E67")])]})]});}
            var Q5;
            Q5=makeQuery(id+"F8.boolean.opBoolean","INTERSECT",EDGE,{"disambiguationData":[OD(0.0)],"derivedFrom":[makeQuery(id+"F5.opExtrude","SWEPT_FACE",FACE,{"disambiguationData":[OSD([sQuery(id+"F4.wireOp",EDGE,"E30")])]}),makeQuery(id+"F8.opExtrude","SWEPT_FACE",FACE,{"disambiguationData":[OSD([sQuery(id+"F7.wireOp",EDGE,"E67")])]})]});
            fillet(context, id + "F14", {"entities" : qUnion([Q0, Q1, Q2, Q3, Q4, Q5]), "radius" : 3 * mm, "tangentPropagation" : true, "allowEdgeOverflow" : false});
        }
        {
            var Q0;
            Q0=makeQuery(id+"F1.opExtrude","CAP_EDGE",EDGE,{"disambiguationData":[OSD([sQuery(id+"F0.wireOp",EDGE,"E1.bottom")])],"isStart":false});
            fillet(context, id + "F15", {"entities" : qUnion([Q0]), "radius" : 2 * mm, "tangentPropagation" : true, "allowEdgeOverflow" : false});
        }
        {
            var Q0;
            {var subQ0=sQuery(id+"F0.wireOp",EDGE,"E21.filletArc");var subQ1=sQuery(id+"F0.wireOp",EDGE,"E7");var subQ2=sQuery(id+"F0.wireOp",EDGE,"E6");var subQ3=sQuery(id+"F0.wireOp",EDGE,"E5");var subQ4=sQuery(id+"F0.wireOp",EDGE,"E4");var subQ5=sQuery(id+"F0.wireOp",EDGE,"E22.filletArc");var subQ6=sQuery(id+"F0.wireOp",EDGE,"E1.bottom");var subQ7=sQuery(id+"F0.wireOp",EDGE,"E1.right");var subQ8=sQuery(id+"F0.wireOp",EDGE,"E1.top");var subQ9=sQuery(id+"F0.wireOp",EDGE,"E1.left");var subQ10=sQuery(id+"F0.wireOp",EDGE,"E23.filletArc");var subQ11=sQuery(id+"F0.wireOp",EDGE,"E24.filletArc");Q0=makeQuery(id+"F2.boolean.opBoolean","SPLIT",FACE,{"disambiguationData":[TD([makeQuery(id+"F1.opExtrude","SWEPT_FACE",FACE,{"disambiguationData":[OSD([subQ6])]})])],"derivedFrom":makeQuery(id+"F1.opExtrude","CAP_FACE",FACE,{"disambiguationData":[OSD([subQ6,subQ8,subQ9,subQ7,subQ4,subQ3,subQ2,subQ1,subQ0,subQ5,subQ10,subQ11])],"isStart":true})});}
            var sketch = newSketch(context, id + "F16", { "sketchPlane" : qUnion([Q0])});
            skLineSegment(sketch, "E79", {"start": v(0, 90) * mm, "end": v(0, 120) * mm, "construction": true});
            skCircle(sketch, "E80", {"center": v(0, 120) * mm, "radius": 6 * mm});
            skLineSegment(sketch, "E81", {"start": v(-27.22, 90) * mm, "end": v(-16.09, 108) * mm});
            skLineSegment(sketch, "E82", {"start": v(-16.09, 108) * mm, "end": v(-16.09, 120.18) * mm});
            skArc(sketch, "E83", {"start": v(-16.09, 120.18) * mm, "mid": v(-0.3, 135.97) * mm, "end": v(15.5, 120.18) * mm});
            skLineSegment(sketch, "E84", {"start": v(15.5, 120.18) * mm, "end": v(15.5, 108.18) * mm});
            skLineSegment(sketch, "E85", {"start": v(15.5, 108.18) * mm, "end": v(33.68, 90) * mm});
            skLineSegment(sketch, "E86", {"start": v(-80, 0) * mm, "end": v(80, 0) * mm, "construction": true});
            skLineSegment(sketch, "E87.MirrorCS", {"start": v(15.5, -120.18) * mm, "end": v(15.5, -108.18) * mm});
            skLineSegment(sketch, "E88.MirrorCS", {"start": v(-16.09, -108) * mm, "end": v(-16.09, -120.18) * mm});
            skLineSegment(sketch, "E89.MirrorCS", {"start": v(15.5, -108.18) * mm, "end": v(33.68, -90) * mm});
            skArc(sketch, "E90.MirrorCS", {"start": v(-16.09, -120.18) * mm, "mid": v(-0.3, -135.97) * mm, "end": v(15.5, -120.18) * mm});
            skLineSegment(sketch, "E91.MirrorCS", {"start": v(-27.22, -90) * mm, "end": v(-16.09, -108) * mm});
            skCircle(sketch, "E92.MirrorC", {"center": v(0, -120) * mm, "radius": 6 * mm});
            skLineSegment(sketch, "E93.MirrorCS", {"start": v(0, -90) * mm, "end": v(0, -120) * mm, "construction": true});
            skSolve(sketch);
        }
        {
            var Q0;
            Q0=makeQuery(id+"F16.imprint","IMPRINT",FACE,{"disambiguationData":[TD([[makeQuery(id+"F16.imprint","IMPRINT",EDGE,{"derivedFrom":sQuery(id+"F16.wireOp",EDGE,"E80")}),-1.0]])]});
            var Q1;
            Q1=makeQuery(id+"F16.imprint","IMPRINT",FACE,{"disambiguationData":[TD([[makeQuery(id+"F16.imprint","IMPRINT",EDGE,{"derivedFrom":sQuery(id+"F16.wireOp",EDGE,"E87.MirrorCS")}),1.0]])]});
            var Q2;
            Q2=makeQuery(id+"F16.imprint","IMPRINT",FACE,{"disambiguationData":[TD([[makeQuery(id+"F16.imprint","IMPRINT",EDGE,{"derivedFrom":makeQuery(id+"F1.opExtrude","CAP_EDGE",EDGE,{"disambiguationData":[OSD([sQuery(id+"F0.wireOp",EDGE,"E1.left")])],"isStart":true})}),-1.0]])]});
            var Q3;
            Q3=makeQuery(id+"F2.opExtrude","CAP_FACE",FACE,{"disambiguationData":[OSD([sQuery(id+"F0.wireOp",EDGE,"E12"),sQuery(id+"F0.wireOp",EDGE,"E13"),sQuery(id+"F0.wireOp",EDGE,"E14"),sQuery(id+"F0.wireOp",EDGE,"E15"),sQuery(id+"F0.wireOp",EDGE,"E17.filletArc"),sQuery(id+"F0.wireOp",EDGE,"E18.filletArc"),sQuery(id+"F0.wireOp",EDGE,"E19.filletArc"),sQuery(id+"F0.wireOp",EDGE,"E20.filletArc"),sQuery(id+"F0.wireOp",EDGE,"E25.0"),sQuery(id+"F0.wireOp",EDGE,"E25.1"),sQuery(id+"F0.wireOp",EDGE,"E25.2"),sQuery(id+"F0.wireOp",EDGE,"E25.3"),sQuery(id+"F0.wireOp",EDGE,"E25.4"),sQuery(id+"F0.wireOp",EDGE,"E25.5"),sQuery(id+"F0.wireOp",EDGE,"E25.6"),sQuery(id+"F0.wireOp",EDGE,"E25.7")])],"isStart":false});
            extrude(context, id + "F17", {"entities" : qUnion([Q0, Q1, Q2]), "endBound" : BoundingType.UP_TO_SURFACE, "endBoundEntityFace" : qUnion([Q3]), "depth" : 25 * mm});
        }
    });
